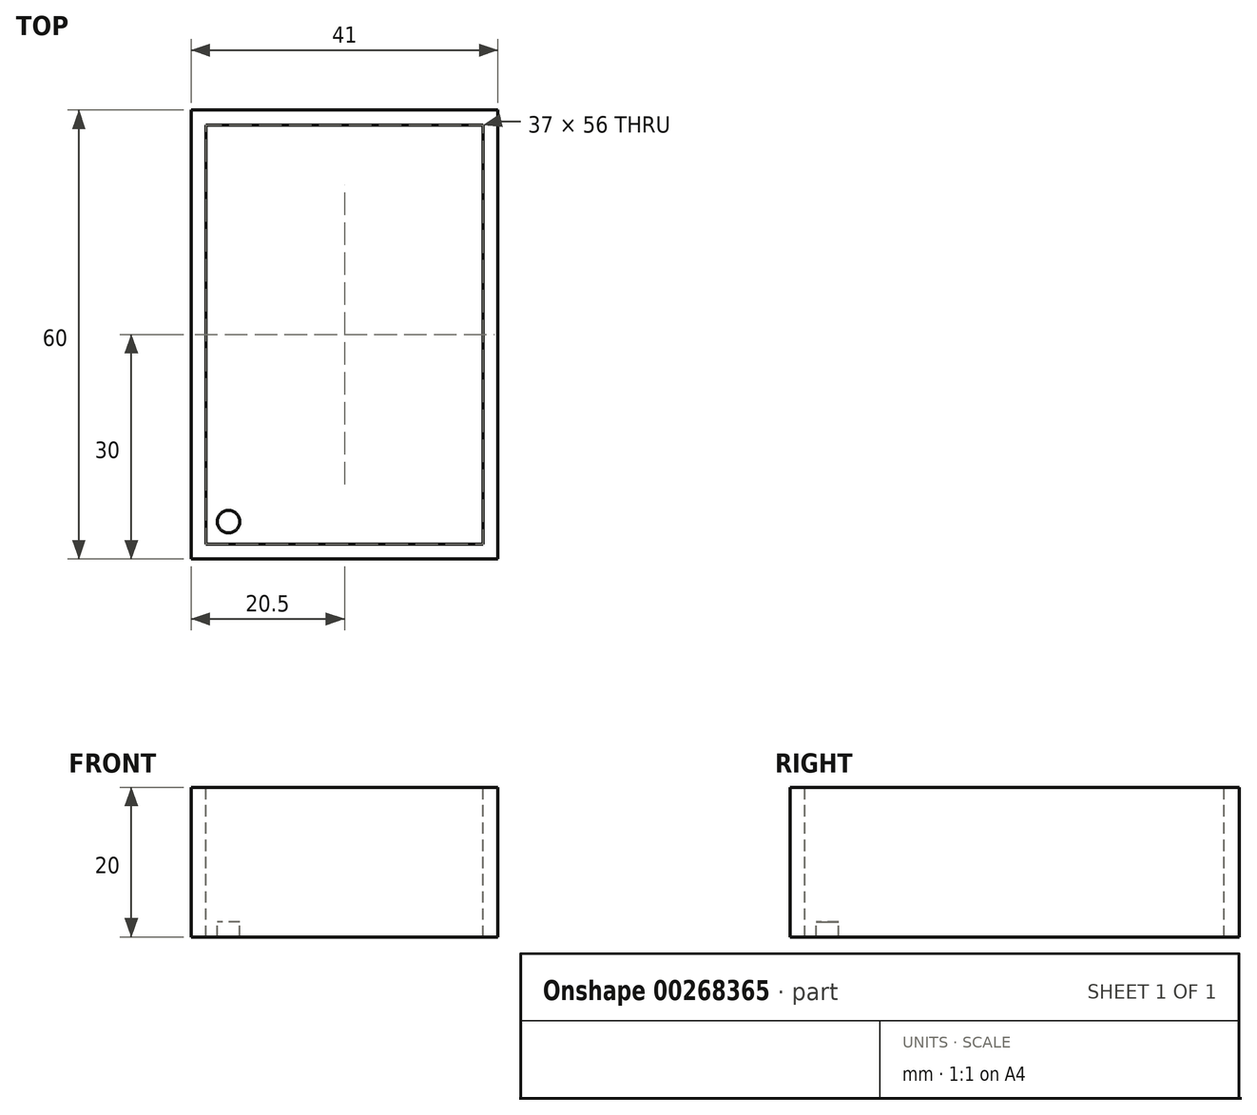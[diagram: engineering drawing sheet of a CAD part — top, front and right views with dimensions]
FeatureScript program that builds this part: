
annotation { "Feature Type Name" : "Feature", "Feature Type Description" : "" }
export const myFeature = defineFeature(function(context is Context, id is Id, definition is map)
    precondition{}
    {
        {
            var Q0;
            Q0=qCreatedBy(makeId("Top.planeOp"),FACE);
            var sketch = newSketch(context, id + "F0", { "sketchPlane" : qUnion([Q0])});
            skLineSegment(sketch, "E0.bottom", {"start": v(-20.5, 30) * mm, "end": v(20.5, 30) * mm});
            skLineSegment(sketch, "E0.top", {"start": v(-20.5, -30) * mm, "end": v(20.5, -30) * mm});
            skLineSegment(sketch, "E0.left", {"start": v(-20.5, 30) * mm, "end": v(-20.5, -30) * mm});
            skLineSegment(sketch, "E0.right", {"start": v(20.5, 30) * mm, "end": v(20.5, -30) * mm});
            skPoint(sketch, "E0.middle", {"position": v(0, 0) * mm});
            skSolve(sketch);
        }
        {
            var Q0;
            Q0 = qSketchRegion(id + "F0", true);
            extrude(context, id + "F1", {"entities" : qUnion([Q0]), "depth" : 20 * mm});
        }
        {
            var Q0;
            Q0=makeQuery(id+"F1.opExtrude","CAP_FACE",FACE,{"disambiguationData":[OSD([sQuery(id+"F0.wireOp",EDGE,"E0.bottom"),sQuery(id+"F0.wireOp",EDGE,"E0.top"),sQuery(id+"F0.wireOp",EDGE,"E0.left"),sQuery(id+"F0.wireOp",EDGE,"E0.right")])],"isStart":false});
            var sketch = newSketch(context, id + "F2", { "sketchPlane" : qUnion([Q0])});
            skLineSegment(sketch, "E1.0", {"start": v(-18.5, 28) * mm, "end": v(-18.5, -28) * mm});
            skLineSegment(sketch, "E1.1", {"start": v(18.5, 28) * mm, "end": v(-18.5, 28) * mm});
            skLineSegment(sketch, "E1.2", {"start": v(18.5, -28) * mm, "end": v(18.5, 28) * mm});
            skLineSegment(sketch, "E1.3", {"start": v(-18.5, -28) * mm, "end": v(18.5, -28) * mm});
            skSolve(sketch);
        }
        {
            var Q0;
            Q0=makeQuery(id+"F2.imprint","IMPRINT",FACE,{"disambiguationData":[TD([[makeQuery(id+"F2.imprint","IMPRINT",EDGE,{"derivedFrom":sQuery(id+"F2.wireOp",EDGE,"E1.0")}),1.0]])]});
            extrude(context, id + "F3", {"entities" : qUnion([Q0]), "operationType" : NewBodyOperationType.REMOVE, "oppositeDirection" : true, "depth" : 18 * mm});
        }
        {
            var Q0;
            Q0=makeQuery(id+"F1.opExtrude","SWEPT_FACE",FACE,{"disambiguationData":[OSD([sQuery(id+"F0.wireOp",EDGE,"E0.left")])]});
            var sketch = newSketch(context, id + "F4", { "sketchPlane" : qUnion([Q0])});
            skLineSegment(sketch, "E2", {"start": v(-30, 16.08) * mm, "end": v(30, 0) * mm, "construction": true});
            skLineSegment(sketch, "E3", {"start": v(-30, 16.08) * mm, "end": v(-30, 0) * mm, "construction": true});
            skLineSegment(sketch, "E4", {"start": v(-30, 0) * mm, "end": v(30, 0) * mm, "construction": true});
            skSolve(sketch);
        }
        {
            var Q0;
            Q0=makeQuery(id+"F3.boolean.opBoolean","COPY",FACE,{"derivedFrom":makeQuery(id+"F3.opExtrude","SWEPT_FACE",FACE,{"disambiguationData":[OSD([sQuery(id+"F2.wireOp",EDGE,"E1.1")])]})});
            var sketch = newSketch(context, id + "F5", { "sketchPlane" : qUnion([Q0])});
            skLineSegment(sketch, "E5", {"start": v(-14.5, 21.08) * mm, "end": v(-14.5, 20) * mm});
            skLineSegment(sketch, "E6", {"start": v(0, 2) * mm, "end": v(0, 20) * mm, "construction": true});
            skLineSegment(sketch, "E7", {"start": v(-14.5, 21.08) * mm, "end": v(-8.5, 21.08) * mm});
            skLineSegment(sketch, "E8", {"start": v(-8.5, 21.08) * mm, "end": v(-8.5, 16.08) * mm});
            skLineSegment(sketch, "E9.MirrorCS", {"start": v(8.5, 21.08) * mm, "end": v(8.5, 16.08) * mm});
            skLineSegment(sketch, "E10.MirrorCS", {"start": v(14.5, 21.08) * mm, "end": v(8.5, 21.08) * mm});
            skLineSegment(sketch, "E11.MirrorCS", {"start": v(14.5, 21.08) * mm, "end": v(14.5, 20) * mm});
            skLineSegment(sketch, "E12", {"start": v(-20.5, 16.08) * mm, "end": v(20.56, 16.08) * mm, "construction": true});
            skSolve(sketch);
        }
        {
            var Q0;
            {var subQ2=sQuery(id+"F5.wireOp",EDGE,"E5");Q0=makeQuery(id+"F5.imprint","IMPRINT",FACE,{"disambiguationData":[TD([[makeQuery(id+"F5.imprint","IMPRINT",EDGE,{"derivedFrom":subQ2}),1.0]])]});}
            extrude(context, id + "F6", {"entities" : qUnion([Q0]), "operationType" : NewBodyOperationType.REMOVE, "oppositeDirection" : true, "depth" : 2 * mm});
        }
        {
            var Q0;
            {var subQ0=sQuery(id+"F2.wireOp",EDGE,"E1.1");var subQ1=makeQuery(id+"F3.boolean.opBoolean","COPY",EDGE,{"derivedFrom":makeQuery(id+"F3.opExtrude","CAP_EDGE",EDGE,{"disambiguationData":[OSD([subQ0])],"isStart":false})});Q0=makeQuery(id+"F6.boolean.opBoolean","MERGE",FACE,{"derivedFrom":[makeQuery(id+"F3.boolean.opBoolean","COPY",FACE,{"derivedFrom":makeQuery(id+"F3.opExtrude","CAP_FACE",FACE,{"disambiguationData":[OSD([sQuery(id+"F2.wireOp",EDGE,"E1.0"),subQ0,sQuery(id+"F2.wireOp",EDGE,"E1.2"),sQuery(id+"F2.wireOp",EDGE,"E1.3")])],"isStart":false})}),makeQuery(id+"F6.opExtrude","SWEPT_FACE",FACE,{"disambiguationData":[OSD([subQ0]),TDD([makeQuery(id+"F5.imprint","IMPRINT",EDGE,{"disambiguationData":[TD([[makeQuery(id+"F5.imprint","INTERSECT",VERTEX,{"derivedFrom":[subQ1,sQuery(id+"F5.wireOp",EDGE,"E8")]}),1.0]])],"derivedFrom":subQ1})])]})]});}
            var sketch = newSketch(context, id + "F7", { "sketchPlane" : qUnion([Q0])});
            skLineSegment(sketch, "E13", {"start": v(-18.5, -25) * mm, "end": v(18.5, -25) * mm, "construction": true});
            skCircle(sketch, "E14", {"center": v(15.5, -25) * mm, "radius": 1.5 * mm});
            skLineSegment(sketch, "E15", {"start": v(0, -28) * mm, "end": v(0, 28) * mm, "construction": true});
            skCircle(sketch, "E16.MirrorC", {"center": v(-15.5, -25) * mm, "radius": 1.5 * mm});
            skSolve(sketch);
        }
        {
            var Q0;
            Q0=makeQuery(id+"F7.imprint","IMPRINT",FACE,{"disambiguationData":[TD([[makeQuery(id+"F7.imprint","IMPRINT",EDGE,{"derivedFrom":sQuery(id+"F7.wireOp",EDGE,"E14")}),1.0]])]});
            var Q1;
            Q1=makeQuery(id+"F7.imprint","IMPRINT",FACE,{"disambiguationData":[TD([[makeQuery(id+"F7.imprint","IMPRINT",EDGE,{"derivedFrom":sQuery(id+"F7.wireOp",EDGE,"E16.MirrorC")}),-1.0]])]});
            extrude(context, id + "F8", {"entities" : qUnion([Q0, Q1]), "operationType" : NewBodyOperationType.REMOVE, "oppositeDirection" : true, "depth" : 2 * mm});
        }
    });
